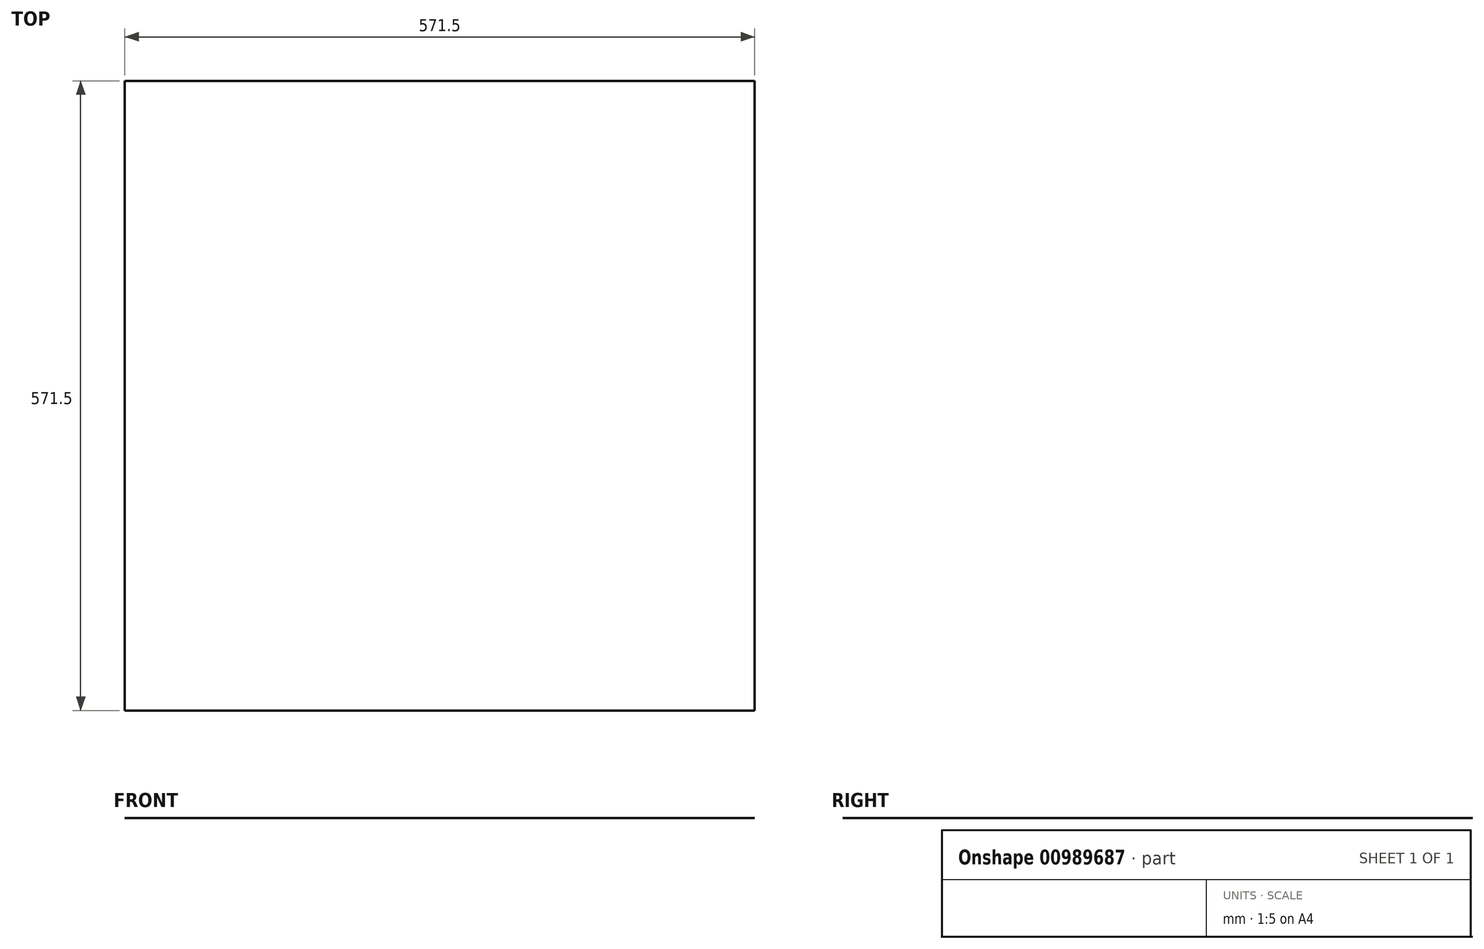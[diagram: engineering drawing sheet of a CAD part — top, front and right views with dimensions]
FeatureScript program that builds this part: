
annotation { "Feature Type Name" : "Feature", "Feature Type Description" : "" }
export const myFeature = defineFeature(function(context is Context, id is Id, definition is map)
    precondition{}
    {
        {
            var Q0;
            Q0=qCreatedBy(makeId("Top.planeOp"),FACE);
            var sketch = newSketch(context, id + "F0", { "sketchPlane" : qUnion([Q0])});
            skLineSegment(sketch, "E0.bottom", {"start": v(-467.13, -292.6) * mm, "end": v(104.37, -292.6) * mm});
            skLineSegment(sketch, "E0.top", {"start": v(-467.13, 278.9) * mm, "end": v(104.37, 278.9) * mm});
            skLineSegment(sketch, "E0.left", {"start": v(-467.13, -292.6) * mm, "end": v(-467.13, 278.9) * mm});
            skLineSegment(sketch, "E0.right", {"start": v(104.37, -292.6) * mm, "end": v(104.37, 278.9) * mm});
            skSolve(sketch);
        }
        {
            var Q0;
            Q0 = qSketchRegion(id + "F0", true);
            extrude(context, id + "F1", {"entities" : qUnion([Q0]), "depth" : 1 / 406.4 * mm, "offsetDistance" : 25.4 * mm});
        }
    });
